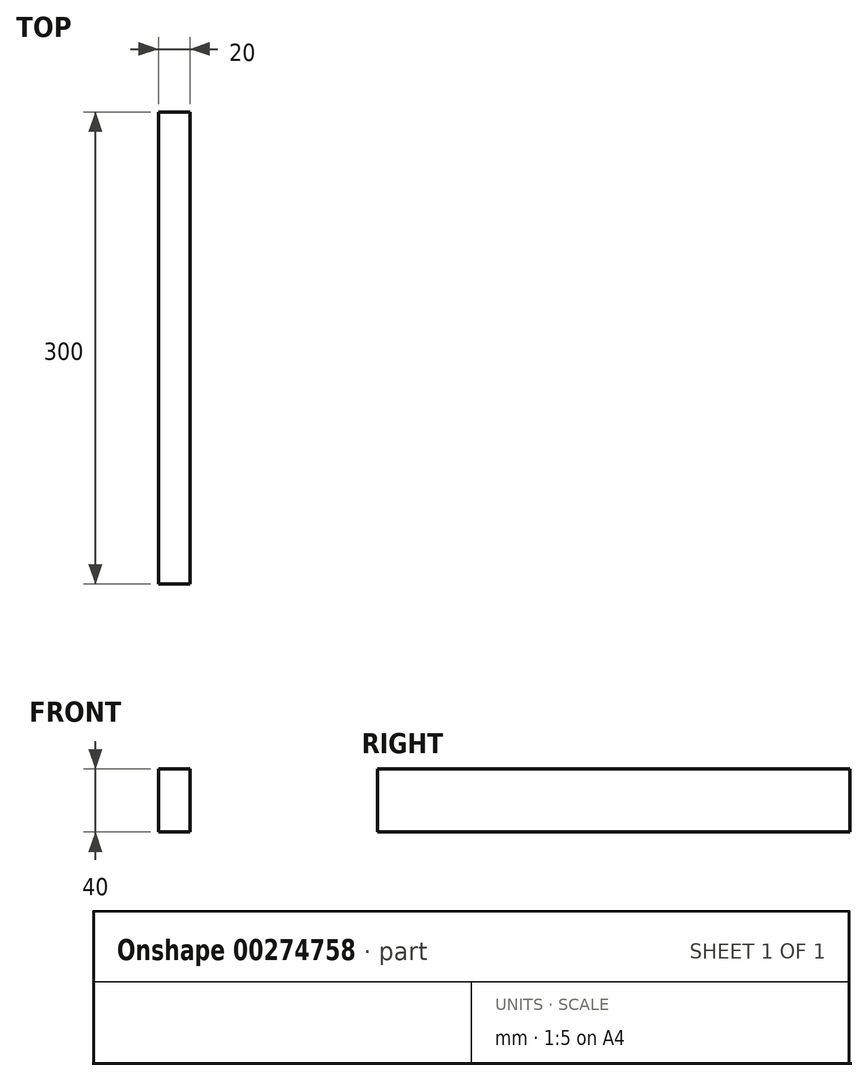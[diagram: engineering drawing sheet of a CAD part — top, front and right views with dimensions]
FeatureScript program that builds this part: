
annotation { "Feature Type Name" : "Feature", "Feature Type Description" : "" }
export const myFeature = defineFeature(function(context is Context, id is Id, definition is map)
    precondition{}
    {
        {
            var Q0;
            Q0=qCreatedBy(makeId("Front.planeOp"),FACE);
            var sketch = newSketch(context, id + "F0", { "sketchPlane" : qUnion([Q0])});
            skLineSegment(sketch, "E0.bottom", {"start": v(-10, 20) * mm, "end": v(10, 20) * mm});
            skLineSegment(sketch, "E0.top", {"start": v(-10, -20) * mm, "end": v(10, -20) * mm});
            skLineSegment(sketch, "E0.left", {"start": v(-10, 20) * mm, "end": v(-10, -20) * mm});
            skLineSegment(sketch, "E0.right", {"start": v(10, 20) * mm, "end": v(10, -20) * mm});
            skSolve(sketch);
        }
        {
            var Q0;
            Q0=makeQuery(id+"F0.imprint","IMPRINT",FACE,{"disambiguationData":[TD([[makeQuery(id+"F0.imprint","IMPRINT",EDGE,{"derivedFrom":sQuery(id+"F0.wireOp",EDGE,"E0.bottom")}),-1.0]])]});
            extrude(context, id + "F1", {"entities" : qUnion([Q0]), "depth" : 300 * mm});
        }
    });
